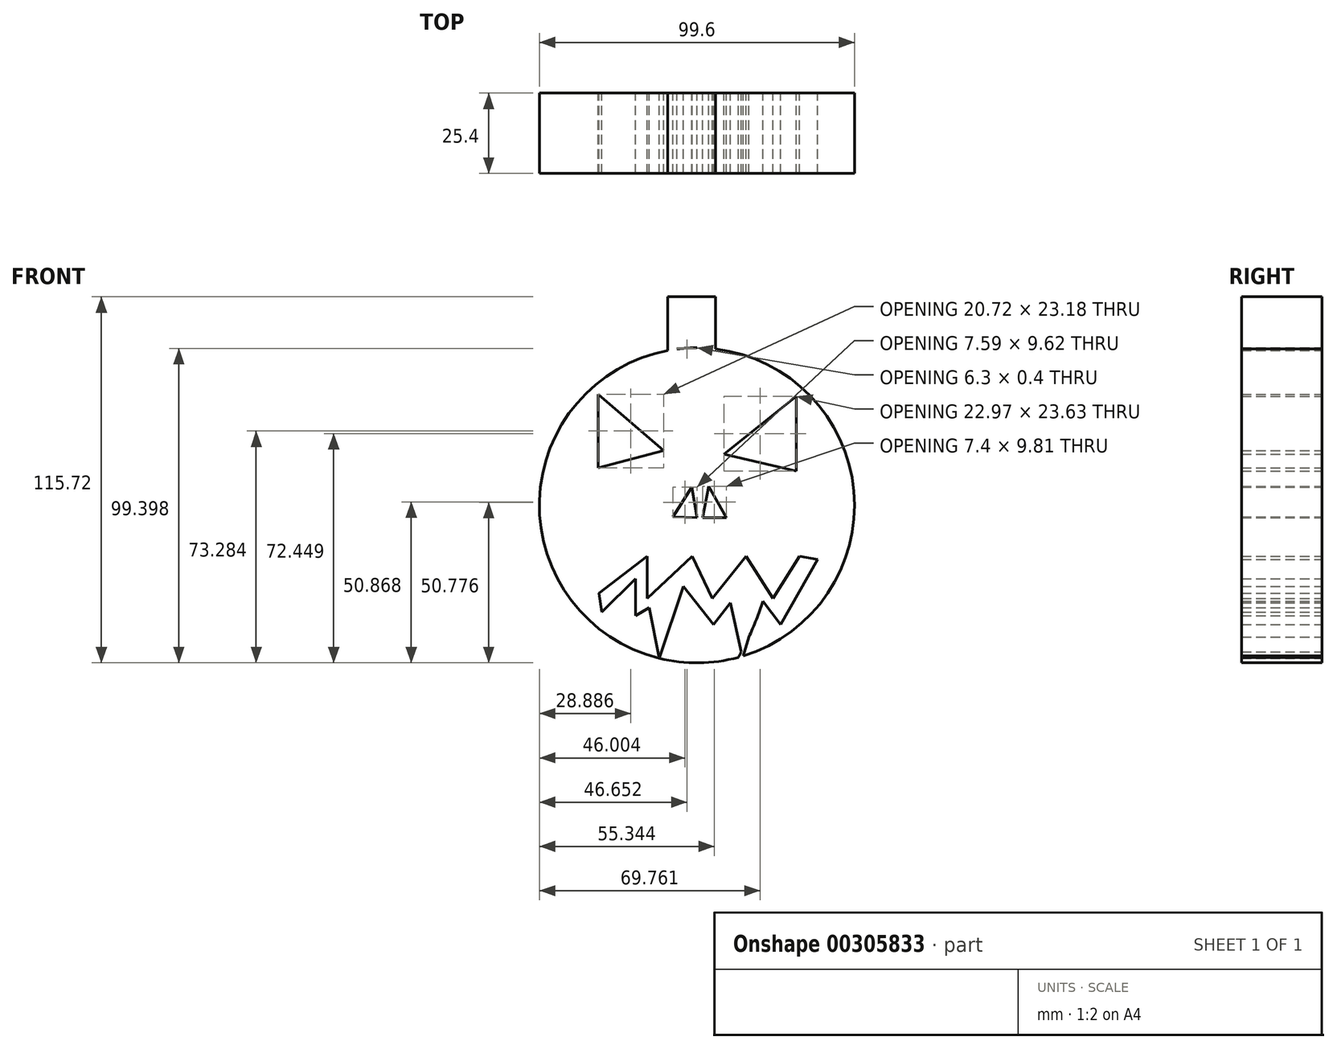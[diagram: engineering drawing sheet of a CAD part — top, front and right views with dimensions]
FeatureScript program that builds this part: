
annotation { "Feature Type Name" : "Feature", "Feature Type Description" : "" }
export const myFeature = defineFeature(function(context is Context, id is Id, definition is map)
    precondition{}
    {
        {
            var Q0;
            Q0=qCreatedBy(makeId("Front.planeOp"),FACE);
            var sketch = newSketch(context, id + "F0", { "sketchPlane" : qUnion([Q0])});
            skCircle(sketch, "E0", {"center": v(0, 0) * mm, "radius": 49.8 * mm});
            skLineSegment(sketch, "E1", {"start": v(-31.27, 35.07) * mm, "end": v(-10.55, 17.26) * mm});
            skLineSegment(sketch, "E2", {"start": v(-31.27, 35.07) * mm, "end": v(-31.27, 11.9) * mm});
            skLineSegment(sketch, "E3", {"start": v(-31.27, 11.9) * mm, "end": v(-10.55, 17.26) * mm});
            skLineSegment(sketch, "E4", {"start": v(31.45, 34.46) * mm, "end": v(31.45, 10.83) * mm});
            skLineSegment(sketch, "E5", {"start": v(31.45, 34.46) * mm, "end": v(8.47, 16.2) * mm});
            skLineSegment(sketch, "E6", {"start": v(8.47, 16.2) * mm, "end": v(31.45, 10.83) * mm});
            skLineSegment(sketch, "E7", {"start": v(-30.93, -27.78) * mm, "end": v(-15.73, -16.04) * mm});
            skLineSegment(sketch, "E8", {"start": v(-15.73, -16.04) * mm, "end": v(-15.73, -29.37) * mm});
            skLineSegment(sketch, "E9", {"start": v(-15.73, -29.37) * mm, "end": v(-1.49, -16.04) * mm});
            skLineSegment(sketch, "E10", {"start": v(-1.49, -16.04) * mm, "end": v(4.8, -29.37) * mm});
            skLineSegment(sketch, "E11", {"start": v(4.8, -29.37) * mm, "end": v(15.54, -16.04) * mm});
            skLineSegment(sketch, "E12", {"start": v(15.54, -16.04) * mm, "end": v(24.05, -29.37) * mm});
            skLineSegment(sketch, "E13", {"start": v(24.05, -29.37) * mm, "end": v(32.37, -16.04) * mm});
            skLineSegment(sketch, "E14", {"start": v(-30.11, -33.68) * mm, "end": v(-19.43, -23.26) * mm});
            skLineSegment(sketch, "E15", {"start": v(-19.43, -23.26) * mm, "end": v(-19.43, -34.92) * mm});
            skLineSegment(sketch, "E16", {"start": v(-19.43, -34.92) * mm, "end": v(-4.26, -25.67) * mm});
            skLineSegment(sketch, "E17", {"start": v(-4.26, -25.67) * mm, "end": v(5.17, -37.7) * mm});
            skLineSegment(sketch, "E18", {"start": v(5.17, -37.7) * mm, "end": v(15.9, -24) * mm});
            skLineSegment(sketch, "E19", {"start": v(15.9, -24) * mm, "end": v(26.45, -37.7) * mm});
            skLineSegment(sketch, "E20", {"start": v(26.45, -37.7) * mm, "end": v(38.1, -17.16) * mm});
            skLineSegment(sketch, "E21", {"start": v(38.1, -17.16) * mm, "end": v(32.37, -16.04) * mm});
            skLineSegment(sketch, "E22", {"start": v(-30.93, -27.78) * mm, "end": v(-30.11, -33.68) * mm});
            skLineSegment(sketch, "E23", {"start": v(-7.6, -3.65) * mm, "end": v(-1.67, 5.79) * mm});
            skLineSegment(sketch, "E24", {"start": v(-1.67, 5.79) * mm, "end": v(0, -3.83) * mm});
            skLineSegment(sketch, "E25", {"start": v(0, -3.83) * mm, "end": v(-7.6, -3.65) * mm});
            skLineSegment(sketch, "E26", {"start": v(1.84, -3.83) * mm, "end": v(3.7, 5.97) * mm});
            skLineSegment(sketch, "E27", {"start": v(3.7, 5.97) * mm, "end": v(9.25, -3.83) * mm});
            skLineSegment(sketch, "E28", {"start": v(9.25, -3.83) * mm, "end": v(1.84, -3.83) * mm});
            skArc(sketch, "E29", {"start": v(-26.19, 42.36) * mm, "mid": v(-41.88, 6.01) * mm, "end": v(-37.04, -33.28) * mm});
            skArc(sketch, "E30", {"start": v(-12.24, 48.27) * mm, "mid": v(-25.83, 3.52) * mm, "end": v(-24.7, -43.24) * mm});
            skLineSegment(sketch, "E31", {"start": v(0, 49.8) * mm, "end": v(0, -49.8) * mm});
            skArc(sketch, "E32", {"start": v(13.06, -48.05) * mm, "mid": v(25.28, 0.6) * mm, "end": v(10.79, 48.62) * mm});
            skArc(sketch, "E33", {"start": v(32.68, -37.58) * mm, "mid": v(42.37, 3.36) * mm, "end": v(26.35, 42.26) * mm});
            skLineSegment(sketch, "E34", {"start": v(-9.18, 48.94) * mm, "end": v(-9.18, 65.92) * mm});
            skLineSegment(sketch, "E35", {"start": v(-9.18, 65.92) * mm, "end": v(5.91, 65.92) * mm});
            skLineSegment(sketch, "E36", {"start": v(5.91, 65.92) * mm, "end": v(5.91, 49.45) * mm});
            skLineSegment(sketch, "E37", {"start": v(-6.3, 65.92) * mm, "end": v(-6.3, 49.4) * mm});
            skLineSegment(sketch, "E38", {"start": v(-6.3, 49.4) * mm, "end": v(0, 49.8) * mm});
            skLineSegment(sketch, "E39", {"start": v(-3.15, 65.92) * mm, "end": v(-3.15, 49.8) * mm});
            skPoint(sketch, "E39.startSnap0", {"position": v(-3.15, 49.6) * mm});
            skLineSegment(sketch, "E40", {"start": v(0, 65.92) * mm, "end": v(0, 49.8) * mm});
            skPoint(sketch, "E40.startSnap0", {"position": v(-1.64, 65.92) * mm});
            skLineSegment(sketch, "E41", {"start": v(3.14, 65.92) * mm, "end": v(3.14, 49.8) * mm});
            skLineSegment(sketch, "E42", {"start": v(13.97, -43.46) * mm, "end": v(14.46, -45.5) * mm});
            skLineSegment(sketch, "E43", {"start": v(14.46, -45.5) * mm, "end": v(20.8, -30.37) * mm});
            skLineSegment(sketch, "E44", {"start": v(-15.73, -29.37) * mm, "end": v(-11.92, -48.35) * mm});
            skLineSegment(sketch, "E45", {"start": v(-11.92, -48.35) * mm, "end": v(-4.26, -25.67) * mm});
            skLineSegment(sketch, "E46", {"start": v(10.54, -30.85) * mm, "end": v(14.46, -48.05) * mm});
            skLineSegment(sketch, "E47", {"start": v(14.46, -48.05) * mm, "end": v(20.04, -29.37) * mm});
            skSolve(sketch);
        }
        {
            var Q0;
            {var subQ0=sQuery(id+"F0.wireOp",EDGE,"E29");Q0=makeQuery(id+"F0.imprint","IMPRINT",FACE,{"disambiguationData":[TD([[makeQuery(id+"F0.imprint","IMPRINT",EDGE,{"derivedFrom":subQ0}),-1.0]])]});}
            var Q1;
            {var subQ11=sQuery(id+"F0.wireOp",EDGE,"E2");Q1=makeQuery(id+"F0.imprint","IMPRINT",FACE,{"disambiguationData":[TD([[makeQuery(id+"F0.imprint","IMPRINT",EDGE,{"derivedFrom":subQ11}),-1.0]])]});}
            var Q2;
            {var subQ10=sQuery(id+"F0.wireOp",EDGE,"E8");Q2=makeQuery(id+"F0.imprint","IMPRINT",FACE,{"disambiguationData":[TD([[makeQuery(id+"F0.imprint","IMPRINT",EDGE,{"derivedFrom":subQ10}),1.0]])]});}
            var Q3;
            {var subQ10=sQuery(id+"F0.wireOp",EDGE,"E4");Q3=makeQuery(id+"F0.imprint","IMPRINT",FACE,{"disambiguationData":[TD([[makeQuery(id+"F0.imprint","IMPRINT",EDGE,{"derivedFrom":subQ10}),1.0]])]});}
            var Q4;
            {var subQ0=sQuery(id+"F0.wireOp",EDGE,"E11");Q4=makeQuery(id+"F0.imprint","IMPRINT",FACE,{"disambiguationData":[TD([[makeQuery(id+"F0.imprint","IMPRINT",EDGE,{"derivedFrom":subQ0}),1.0]])]});}
            var Q5;
            {var subQ0=sQuery(id+"F0.wireOp",EDGE,"E33");Q5=makeQuery(id+"F0.imprint","IMPRINT",FACE,{"disambiguationData":[TD([[makeQuery(id+"F0.imprint","IMPRINT",EDGE,{"derivedFrom":subQ0}),-1.0]])]});}
            var Q6;
            {var subQ0=sQuery(id+"F0.wireOp",EDGE,"E15");Q6=makeQuery(id+"F0.imprint","IMPRINT",FACE,{"disambiguationData":[TD([[makeQuery(id+"F0.imprint","IMPRINT",EDGE,{"derivedFrom":subQ0}),-1.0]])]});}
            var Q7;
            {var subQ0=sQuery(id+"F0.wireOp",EDGE,"E34");Q7=makeQuery(id+"F0.imprint","IMPRINT",FACE,{"disambiguationData":[TD([[makeQuery(id+"F0.imprint","IMPRINT",EDGE,{"derivedFrom":subQ0}),-1.0]])]});}
            var Q8;
            {var subQ3=sQuery(id+"F0.wireOp",EDGE,"E37");Q8=makeQuery(id+"F0.imprint","IMPRINT",FACE,{"disambiguationData":[TD([[makeQuery(id+"F0.imprint","IMPRINT",EDGE,{"derivedFrom":subQ3}),1.0]])]});}
            var Q9;
            {var subQ0=sQuery(id+"F0.wireOp",EDGE,"E36");Q9=makeQuery(id+"F0.imprint","IMPRINT",FACE,{"disambiguationData":[TD([[makeQuery(id+"F0.imprint","IMPRINT",EDGE,{"derivedFrom":subQ0}),-1.0]])]});}
            var Q10;
            {var subQ3=sQuery(id+"F0.wireOp",EDGE,"E45");Q10=makeQuery(id+"F0.imprint","IMPRINT",FACE,{"disambiguationData":[TD([[makeQuery(id+"F0.imprint","IMPRINT",EDGE,{"derivedFrom":subQ3}),-1.0]])]});}
            var Q11;
            {var subQ5=sQuery(id+"F0.wireOp",EDGE,"E31");var subQ7=sQuery(id+"F0.wireOp",EDGE,"E0");var subQ8=makeQuery(id+"F0.imprint","INTERSECT",VERTEX,{"derivedFrom":[subQ7,subQ5]});Q11=makeQuery(id+"F0.imprint","IMPRINT",FACE,{"disambiguationData":[TD([[makeQuery(id+"F0.imprint","IMPRINT",EDGE,{"disambiguationData":[TD([[subQ8,-1.0]])],"derivedFrom":subQ7}),1.0]])]});}
            extrude(context, id + "F1", {"entities" : qUnion([Q0, Q1, Q2, Q3, Q4, Q5, Q6, Q7, Q8, Q9, Q10, Q11]), "depth" : 25.4 * mm});
        }
    });
